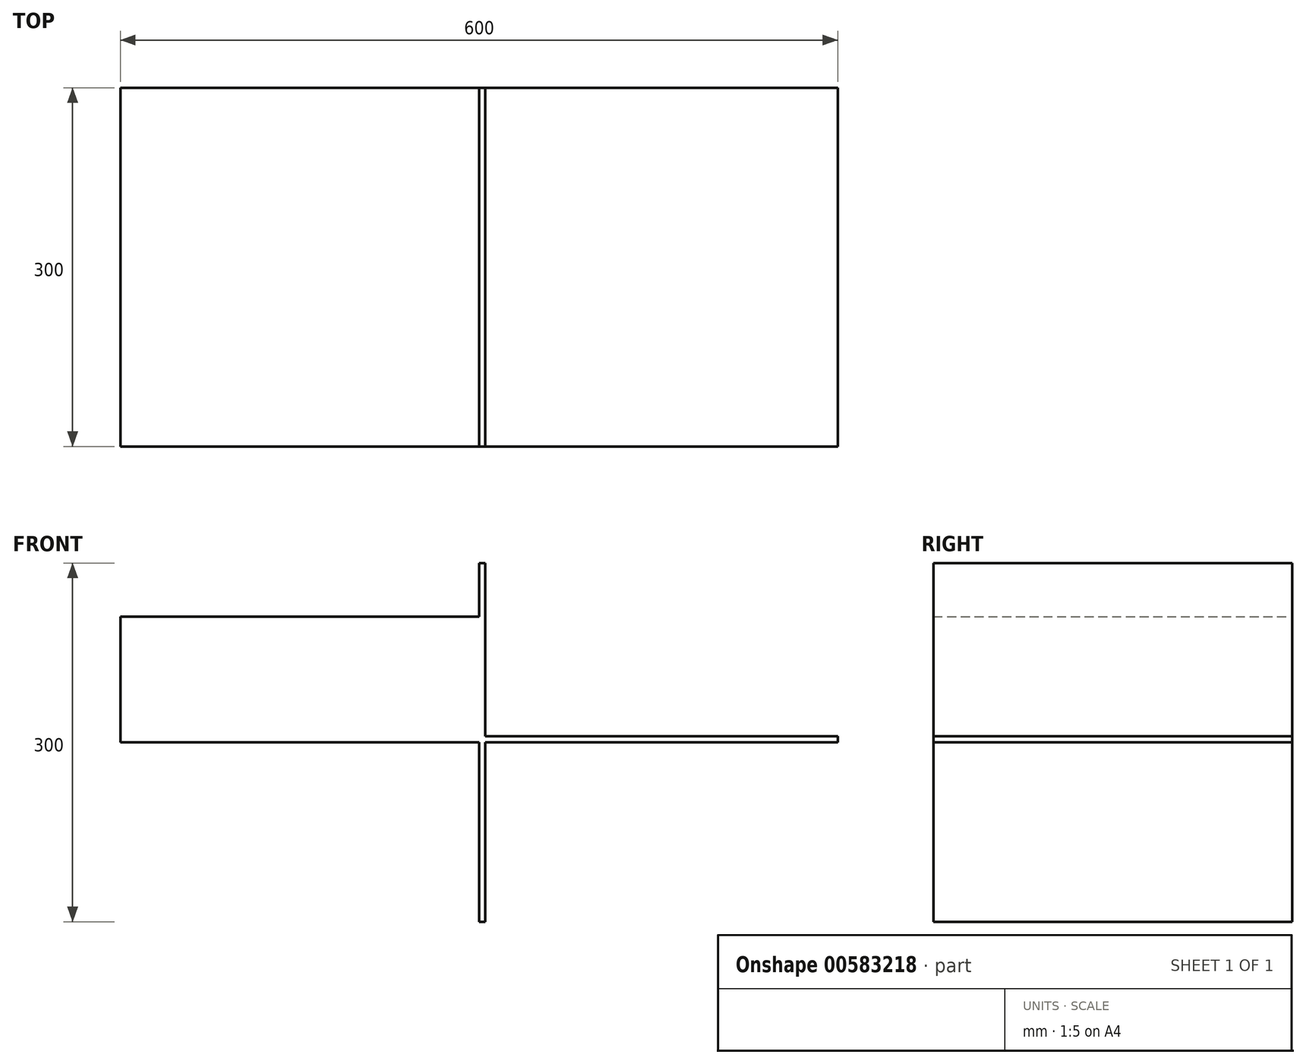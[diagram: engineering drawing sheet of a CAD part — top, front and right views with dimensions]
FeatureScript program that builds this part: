
annotation { "Feature Type Name" : "Feature", "Feature Type Description" : "" }
export const myFeature = defineFeature(function(context is Context, id is Id, definition is map)
    precondition{}
    {
        {
            var Q0;
            Q0=qCreatedBy(makeId("Top.planeOp"),FACE);
            var sketch = newSketch(context, id + "F0", { "sketchPlane" : qUnion([Q0])});
            skLineSegment(sketch, "E0.bottom", {"start": v(300, 150) * mm, "end": v(-300, 150) * mm});
            skLineSegment(sketch, "E0.top", {"start": v(300, -150) * mm, "end": v(-300, -150) * mm});
            skLineSegment(sketch, "E0.left", {"start": v(300, 150) * mm, "end": v(300, -150) * mm});
            skLineSegment(sketch, "E0.right", {"start": v(-300, 150) * mm, "end": v(-300, -150) * mm});
            skPoint(sketch, "E0.middle", {"position": v(0, 0) * mm});
            skSolve(sketch);
        }
        {
            var Q0;
            Q0=makeQuery(id+"F0.imprint","IMPRINT",FACE,{"disambiguationData":[TD([[makeQuery(id+"F0.imprint","IMPRINT",EDGE,{"derivedFrom":sQuery(id+"F0.wireOp",EDGE,"E0.bottom")}),1.0]])]});
            extrude(context, id + "F1", {"entities" : qUnion([Q0]), "depth" : 5 * mm, "offsetDistance" : 25.4 * mm});
        }
        {
            var Q0;
            Q0=qCreatedBy(makeId("Right.planeOp"),FACE);
            var sketch = newSketch(context, id + "F2", { "sketchPlane" : qUnion([Q0])});
            skLineSegment(sketch, "E1.bottom", {"start": v(150, -150) * mm, "end": v(-150, -150) * mm});
            skLineSegment(sketch, "E1.top", {"start": v(150, 150) * mm, "end": v(-150, 150) * mm});
            skLineSegment(sketch, "E1.left", {"start": v(150, -150) * mm, "end": v(150, 150) * mm});
            skLineSegment(sketch, "E1.right", {"start": v(-150, -150) * mm, "end": v(-150, 150) * mm});
            skPoint(sketch, "E1.middle", {"position": v(0, 0) * mm});
            skSolve(sketch);
        }
        {
            var Q0;
            Q0 = qSketchRegion(id + "F2", true);
            extrude(context, id + "F3", {"entities" : qUnion([Q0]), "operationType" : NewBodyOperationType.ADD, "depth" : 5 * mm, "offsetDistance" : 25.4 * mm});
        }
        {
            var Q0;
            {var subQ0=sQuery(id+"F2.wireOp",EDGE,"E1.top");var subQ3=sQuery(id+"F2.wireOp",EDGE,"E1.left");var subQ4=sQuery(id+"F2.wireOp",EDGE,"E1.right");Q0=makeQuery(id+"F3.boolean.opBoolean","SPLIT",FACE,{"disambiguationData":[TD([makeQuery(id+"F3.opExtrude","SWEPT_FACE",FACE,{"disambiguationData":[OSD([subQ0])]})])],"derivedFrom":makeQuery(id+"F3.opExtrude","CAP_FACE",FACE,{"disambiguationData":[OSD([sQuery(id+"F2.wireOp",EDGE,"E1.bottom"),subQ0,subQ3,subQ4])],"isStart":false})});}
            var sketch = newSketch(context, id + "F4", { "sketchPlane" : qUnion([Q0])});
            skCircle(sketch, "E2", {"center": v(-31.17, 100.14) * mm, "radius": 20.77 * mm});
            skSolve(sketch);
        }
        {
            var Q0;
            Q0=sQuery(id+"F4.wireOp",EDGE,"E2");
            extrude(context, id + "F5", {"bodyType" : ToolBodyType.SURFACE, "surfaceEntities" : qUnion([Q0]), "endBound" : BoundingType.SYMMETRIC, "depth" : 300 * mm, "offsetDistance" : 25.4 * mm});
        }
        {
            var Q0;
            {var subQ2=sQuery(id+"F0.wireOp",EDGE,"E0.top");var subQ3=sQuery(id+"F0.wireOp",EDGE,"E0.right");var subQ4=sQuery(id+"F0.wireOp",EDGE,"E0.bottom");Q0=makeQuery(id+"F3.boolean.opBoolean","SPLIT",FACE,{"disambiguationData":[TD([makeQuery(id+"F1.opExtrude","SWEPT_FACE",FACE,{"disambiguationData":[OSD([subQ3])]})])],"derivedFrom":makeQuery(id+"F1.opExtrude","CAP_FACE",FACE,{"disambiguationData":[OSD([subQ4,subQ2,sQuery(id+"F0.wireOp",EDGE,"E0.left"),subQ3])],"isStart":false})});}
            var sketch = newSketch(context, id + "F6", { "sketchPlane" : qUnion([Q0])});
            skLineSegment(sketch, "E3.bottom", {"start": v(-465.7, 24.6) * mm, "end": v(-655.19, 24.6) * mm});
            skLineSegment(sketch, "E3.top", {"start": v(-465.7, 168.46) * mm, "end": v(-655.19, 168.46) * mm});
            skLineSegment(sketch, "E3.left", {"start": v(-465.7, 24.6) * mm, "end": v(-465.7, 168.46) * mm});
            skLineSegment(sketch, "E3.right", {"start": v(-655.19, 24.6) * mm, "end": v(-655.19, 168.46) * mm});
            skPoint(sketch, "E3.middle", {"position": v(-560.44, 96.53) * mm});
            skSolve(sketch);
        }
        {
            var Q0;
            {var subQ0=sQuery(id+"F0.wireOp",EDGE,"E0.right");Q0=makeQuery(id+"F6.imprint","IMPRINT",FACE,{"disambiguationData":[TD([[makeQuery(id+"F6.imprint","IMPRINT",EDGE,{"derivedFrom":makeQuery(id+"F1.opExtrude","CAP_EDGE",EDGE,{"disambiguationData":[OSD([subQ0])],"isStart":false})}),1.0]])]});}
            extrude(context, id + "F7", {"entities" : qUnion([Q0]), "operationType" : NewBodyOperationType.ADD, "depth" : 100 * mm, "offsetDistance" : 25.4 * mm});
        }
    });
